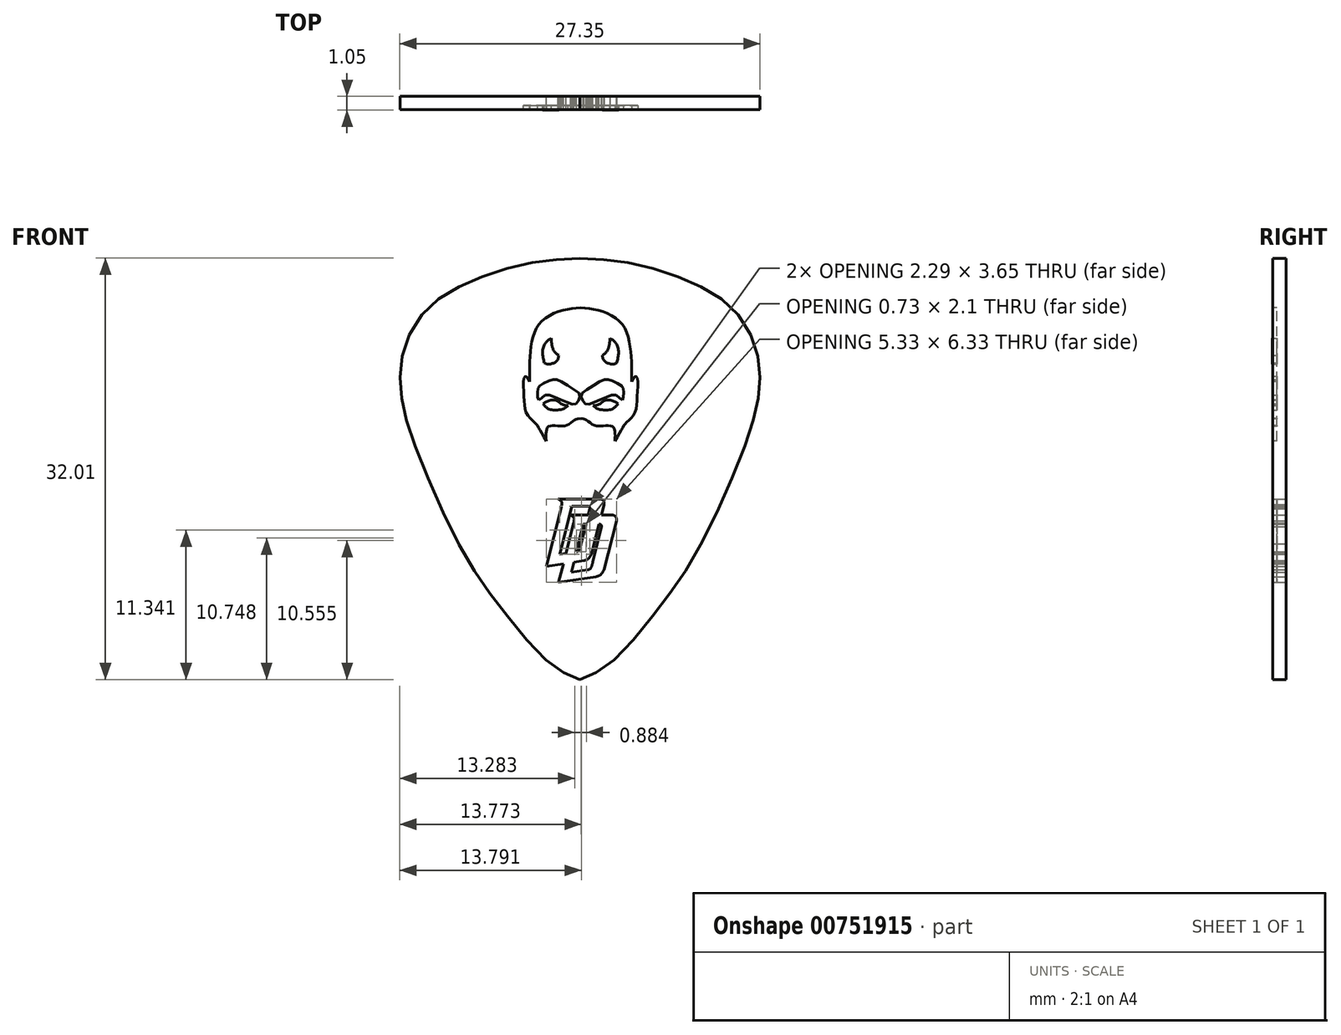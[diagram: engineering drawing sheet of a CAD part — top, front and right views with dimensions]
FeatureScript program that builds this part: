
annotation { "Feature Type Name" : "Feature", "Feature Type Description" : "" }
export const myFeature = defineFeature(function(context is Context, id is Id, definition is map)
    precondition{}
    {
        {
            var Q0;
            Q0=qCreatedBy(makeId("Front.planeOp"),FACE);
            var sketch = newSketch(context, id + "F0", { "sketchPlane" : qUnion([Q0])});
            skFitSpline(sketch, "E0.MirrorCS", {"points": [v(-31.51, -10.9) * mm, v(-29.34, -9.79) * mm, v(-25.56, -5.52) * mm, v(-22.46, -0.91) * mm, v(-18.88, 7.14) * mm, v(-17.9, 10.9) * mm, v(-18.08, 14) * mm, v(-19.85, 17.2) * mm, v(-23.08, 19.28) * mm, v(-27.51, 20.7) * mm, v(-31.51, 21.1) * mm], "startDerivative": vector(27.97, 10.13) * mm, "endDerivative": vector(-41.25, 2.12) * mm});
            skFitSpline(sketch, "E1.MirrorCS", {"points": [v(-31.51, -10.9) * mm, v(-33.68, -9.79) * mm, v(-37.46, -5.52) * mm, v(-40.56, -0.91) * mm, v(-44.14, 7.14) * mm, v(-45.12, 10.9) * mm, v(-44.94, 14) * mm, v(-43.17, 17.2) * mm, v(-39.94, 19.28) * mm, v(-35.5, 20.7) * mm, v(-31.51, 21.1) * mm], "startDerivative": vector(-27.97, 10.13) * mm, "endDerivative": vector(41.25, 2.12) * mm});
            skSolve(sketch);
        }
        {
            var Q0;
            Q0 = qSketchRegion(id + "F0", true);
            var Q1;
            Q1=makeQuery(id+"F0.imprint","IMPRINT",FACE,{"disambiguationData":[TD([[makeQuery(id+"F0.imprint","IMPRINT",EDGE,{"derivedFrom":sQuery(id+"F0.wireOp",EDGE,"E0.MirrorCS")}),1.0]])]});
            extrude(context, id + "F1", {"entities" : qUnion([Q0, Q1]), "depth" : 1 * mm, "offsetDistance" : 25.4 * mm});
        }
        {
            var Q0;
            Q0=qCreatedBy(makeId("Front.planeOp"),FACE);
            var sketch = newSketch(context, id + "F2", { "sketchPlane" : qUnion([Q0])});
            skLineSegment(sketch, "E2", {"start": v(-33.17, 2.8) * mm, "end": v(-30.14, 2.8) * mm});
            skFitSpline(sketch, "E3", {"points": [v(-33.17, 2.8) * mm, v(-32.99, 2.69) * mm, v(-32.9, 2.56) * mm, v(-32.92, 2.2) * mm], "startDerivative": vector(0.59, -0.39) * mm, "endDerivative": vector(-0.18, -0.99) * mm});
            skLineSegment(sketch, "E4", {"start": v(-32.92, 2.2) * mm, "end": v(-34.07, -2.3) * mm});
            skLineSegment(sketch, "E5", {"start": v(-29.68, 2.37) * mm, "end": v(-29.87, 1.6) * mm});
            skFitSpline(sketch, "E6", {"points": [v(-29.68, 2.37) * mm, v(-29.68, 2.56) * mm, v(-29.81, 2.75) * mm, v(-30.14, 2.8) * mm], "startDerivative": vector(0.08, 0.64) * mm, "endDerivative": vector(-0.94, 0.02) * mm});
            skLineSegment(sketch, "E7", {"start": v(-34.07, -2.3) * mm, "end": v(-32.77, -2.11) * mm});
            skFitSpline(sketch, "E8", {"points": [v(-31.2, -1.88) * mm, v(-30.9, -1.75) * mm, v(-30.62, -1.35) * mm], "startDerivative": vector(0.73, 0.2) * mm, "endDerivative": vector(0.45, 0.85) * mm});
            skLineSegment(sketch, "E9", {"start": v(-32.23, 1.6) * mm, "end": v(-30.88, 1.6) * mm});
            skFitSpline(sketch, "E10", {"points": [v(-32.23, 1.6) * mm, v(-32.05, 1.47) * mm, v(-31.96, 1.35) * mm, v(-31.98, 1) * mm], "startDerivative": vector(0.59, -0.39) * mm, "endDerivative": vector(-0.18, -0.99) * mm});
            skLineSegment(sketch, "E11", {"start": v(-31.98, 1) * mm, "end": v(-32.57, -1.33) * mm});
            skLineSegment(sketch, "E12", {"start": v(-28.74, 1.16) * mm, "end": v(-29.68, -2.56) * mm});
            skFitSpline(sketch, "E13", {"points": [v(-28.74, 1.16) * mm, v(-28.74, 1.35) * mm, v(-28.88, 1.54) * mm, v(-29.2, 1.6) * mm], "startDerivative": vector(0.08, 0.64) * mm, "endDerivative": vector(-0.94, 0.02) * mm});
            skLineSegment(sketch, "E14", {"start": v(-33.13, -3.52) * mm, "end": v(-30.27, -3.1) * mm});
            skFitSpline(sketch, "E15", {"points": [v(-30.27, -3.1) * mm, v(-29.95, -2.96) * mm, v(-29.68, -2.56) * mm], "startDerivative": vector(0.73, 0.2) * mm, "endDerivative": vector(0.45, 0.85) * mm});
            skLineSegment(sketch, "E16", {"start": v(-32.14, 2.25) * mm, "end": v(-33.05, -1.4) * mm});
            skLineSegment(sketch, "E17", {"start": v(-33.05, -1.4) * mm, "end": v(-32.57, -1.33) * mm});
            skFitSpline(sketch, "E18", {"points": [v(-31.82, -1.22) * mm, v(-31.65, -1.17) * mm, v(-31.5, -0.94) * mm, v(-31.41, -0.6) * mm], "startDerivative": vector(0.63, 0.09) * mm, "endDerivative": vector(0.2, 0.9) * mm});
            skLineSegment(sketch, "E19", {"start": v(-31.41, -0.6) * mm, "end": v(-31.05, 0.89) * mm});
            skLineSegment(sketch, "E20", {"start": v(-32.14, 2.25) * mm, "end": v(-30.94, 2.25) * mm});
            skFitSpline(sketch, "E21", {"points": [v(-30.77, 2.07) * mm, v(-30.77, 2.15) * mm, v(-30.83, 2.24) * mm, v(-30.94, 2.25) * mm], "startDerivative": vector(0.04, 0.26) * mm, "endDerivative": vector(-0.34, 0) * mm});
            skLineSegment(sketch, "E22", {"start": v(-31.25, 0.89) * mm, "end": v(-31.78, -1.21) * mm});
            skLineSegment(sketch, "E23", {"start": v(-32.17, -2.76) * mm, "end": v(-30.93, -2.58) * mm});
            skFitSpline(sketch, "E24", {"points": [v(-30.93, -2.58) * mm, v(-30.77, -2.53) * mm, v(-30.63, -2.31) * mm, v(-30.53, -1.97) * mm], "startDerivative": vector(0.63, 0.09) * mm, "endDerivative": vector(0.2, 0.9) * mm});
            skLineSegment(sketch, "E25", {"start": v(-30.53, -1.97) * mm, "end": v(-29.88, 0.7) * mm});
            skLineSegment(sketch, "E26", {"start": v(-31.25, 0.89) * mm, "end": v(-31.05, 0.89) * mm});
            skFitSpline(sketch, "E27", {"points": [v(-29.88, 0.7) * mm, v(-29.88, 0.79) * mm, v(-29.94, 0.87) * mm, v(-30.06, 0.89) * mm], "startDerivative": vector(0.04, 0.26) * mm, "endDerivative": vector(-0.34, 0) * mm});
            skLineSegment(sketch, "E28.trimOffspring", {"start": v(-31.98, -2) * mm, "end": v(-32.17, -2.76) * mm});
            skLineSegment(sketch, "E29.trimOffspring", {"start": v(-32.77, -2.11) * mm, "end": v(-33.13, -3.52) * mm});
            skLineSegment(sketch, "E30.trimOffspring", {"start": v(-31.98, -2) * mm, "end": v(-31.2, -1.88) * mm});
            skLineSegment(sketch, "E31.trimOffspring", {"start": v(-30.88, 1.6) * mm, "end": v(-30.77, 2.07) * mm});
            skLineSegment(sketch, "E32.trimOffspring", {"start": v(-29.87, 1.6) * mm, "end": v(-29.2, 1.6) * mm});
            skLineSegment(sketch, "E33.trimOffspring", {"start": v(-30.05, 0.89) * mm, "end": v(-30.62, -1.35) * mm});
            skSolve(sketch);
        }
        {
            var Q0;
            Q0 = qSketchRegion(id + "F2", true);
            extrude(context, id + "F3", {"entities" : qUnion([Q0]), "operationType" : NewBodyOperationType.REMOVE, "endBound" : BoundingType.THROUGH_ALL, "depth" : 25.4 * mm, "offsetDistance" : 25.4 * mm, "hasSecondDirection" : true, "secondDirectionOppositeDirection" : true, "secondDirectionDepth" : .2 * mm});
        }
        {
            var Q0;
            {var subQ0=sQuery(id+"F0.wireOp",EDGE,"E1.MirrorCS");var subQ1=sQuery(id+"F0.wireOp",EDGE,"E0.MirrorCS");Q0=makeQuery(id+"F3.boolean.opBoolean","SPLIT",FACE,{"disambiguationData":[TD([makeQuery(id+"F1.opExtrude","SWEPT_FACE",FACE,{"disambiguationData":[OSD([subQ1])]})])],"derivedFrom":makeQuery(id+"F1.opExtrude","CAP_FACE",FACE,{"disambiguationData":[OSD([subQ1,subQ0])],"isStart":false})});}
            var sketch = newSketch(context, id + "F4", { "sketchPlane" : qUnion([Q0])});
            skFitSpline(sketch, "E34", {"points": [v(-34.07, 7.22) * mm, v(-34.62, 8.16) * mm, v(-34.8, 8.44) * mm, v(-35.12, 8.77) * mm, v(-35.6, 9.37) * mm, v(-35.75, 10.44) * mm, v(-35.79, 11.87) * mm, v(-35.64, 12.13) * mm, v(-35.33, 11.72) * mm], "startDerivative": vector(-4.06, 6.89) * mm, "endDerivative": vector(3.02, -5.65) * mm});
            skFitSpline(sketch, "E35", {"points": [v(-35.33, 11.72) * mm, v(-35.33, 12.86) * mm, v(-35.17, 14.74) * mm, v(-34.5, 16.22) * mm, v(-32.98, 17.1) * mm, v(-31.46, 17.34) * mm], "startDerivative": vector(-0.08, 6.2) * mm, "endDerivative": vector(7.58, 0.61) * mm});
            skFitSpline(sketch, "E36.MirrorCS", {"points": [v(-27.59, 11.72) * mm, v(-27.59, 12.86) * mm, v(-27.76, 14.74) * mm, v(-28.43, 16.22) * mm, v(-29.94, 17.1) * mm, v(-31.46, 17.34) * mm], "startDerivative": vector(0.08, 6.2) * mm, "endDerivative": vector(-7.58, 0.61) * mm});
            skFitSpline(sketch, "E37.MirrorCS", {"points": [v(-28.85, 7.22) * mm, v(-28.3, 8.16) * mm, v(-28.13, 8.44) * mm, v(-27.8, 8.77) * mm, v(-27.33, 9.37) * mm, v(-27.17, 10.44) * mm, v(-27.13, 11.87) * mm, v(-27.28, 12.13) * mm, v(-27.59, 11.72) * mm], "startDerivative": vector(4.06, 6.89) * mm, "endDerivative": vector(-3.02, -5.65) * mm});
            skFitSpline(sketch, "E38", {"points": [v(-34.07, 7.22) * mm, v(-34.07, 7.92) * mm, v(-33.92, 8.29) * mm, v(-33.34, 8.37) * mm, v(-32.67, 8.36) * mm, v(-32.1, 8.65) * mm, v(-31.72, 8.9) * mm, v(-31.46, 8.9) * mm], "startDerivative": vector(-0.18, 4.45) * mm, "endDerivative": vector(2.53, -0.4) * mm});
            skFitSpline(sketch, "E39.MirrorCS", {"points": [v(-28.85, 7.22) * mm, v(-28.85, 7.92) * mm, v(-29, 8.29) * mm, v(-29.58, 8.37) * mm, v(-30.26, 8.36) * mm, v(-30.82, 8.65) * mm, v(-31.2, 8.9) * mm, v(-31.46, 8.9) * mm], "startDerivative": vector(0.18, 4.45) * mm, "endDerivative": vector(-2.53, -0.4) * mm});
            skSolve(sketch);
        }
        {
            var Q0;
            Q0 = qSketchRegion(id + "F4", true);
            extrude(context, id + "F5", {"entities" : qUnion([Q0]), "operationType" : NewBodyOperationType.REMOVE, "oppositeDirection" : true, "depth" : .3 * mm, "offsetDistance" : 25 * mm});
        }
        {
            var Q0;
            Q0=makeQuery(id+"F5.boolean.opBoolean","COPY",FACE,{"derivedFrom":makeQuery(id+"F5.opExtrude","CAP_FACE",FACE,{"disambiguationData":[OSD([sQuery(id+"F4.wireOp",EDGE,"E34"),sQuery(id+"F4.wireOp",EDGE,"E35"),sQuery(id+"F4.wireOp",EDGE,"E36.MirrorCS"),sQuery(id+"F4.wireOp",EDGE,"E37.MirrorCS"),sQuery(id+"F4.wireOp",EDGE,"E38"),sQuery(id+"F4.wireOp",EDGE,"E39.MirrorCS")])],"isStart":false})});
            var sketch = newSketch(context, id + "F6", { "sketchPlane" : qUnion([Q0])});
            skFitSpline(sketch, "E40", {"points": [v(-33.12, 13.73) * mm, v(-33.52, 14.1) * mm, v(-33.7, 15.01) * mm], "startDerivative": vector(-1.04, 0.7) * mm, "endDerivative": vector(-0.15, 1.82) * mm});
            skFitSpline(sketch, "E41", {"points": [v(-33.7, 15.01) * mm, v(-34.13, 14.66) * mm, v(-34.35, 14) * mm, v(-34.2, 13.13) * mm], "startDerivative": vector(-1.6, -1.02) * mm, "endDerivative": vector(0.6, -2.38) * mm});
            skFitSpline(sketch, "E42", {"points": [v(-34.2, 13.13) * mm, v(-33.97, 13.06) * mm, v(-33.51, 13.13) * mm, v(-33.19, 13.4) * mm, v(-33.12, 13.73) * mm], "startDerivative": vector(1.03, -0.49) * mm, "endDerivative": vector(0.1, 1.39) * mm});
            skFitSpline(sketch, "E43.MirrorCS", {"points": [v(-29.8, 13.73) * mm, v(-29.4, 14.1) * mm, v(-29.23, 15.01) * mm], "startDerivative": vector(1.04, 0.7) * mm, "endDerivative": vector(0.15, 1.82) * mm});
            skFitSpline(sketch, "E44.MirrorCS", {"points": [v(-29.23, 15.01) * mm, v(-28.8, 14.66) * mm, v(-28.57, 14) * mm, v(-28.71, 13.13) * mm], "startDerivative": vector(1.6, -1.02) * mm, "endDerivative": vector(-0.6, -2.38) * mm});
            skFitSpline(sketch, "E45.MirrorCS", {"points": [v(-28.71, 13.13) * mm, v(-28.95, 13.06) * mm, v(-29.4, 13.13) * mm, v(-29.73, 13.4) * mm, v(-29.8, 13.73) * mm], "startDerivative": vector(-1.03, -0.49) * mm, "endDerivative": vector(-0.1, 1.39) * mm});
            skSolve(sketch);
        }
        {
            var Q0;
            Q0=makeQuery(id+"F6.imprint","IMPRINT",FACE,{"disambiguationData":[TD([[makeQuery(id+"F6.imprint","IMPRINT",EDGE,{"derivedFrom":sQuery(id+"F6.wireOp",EDGE,"E43.MirrorCS")}),-1.0]])]});
            var Q1;
            Q1=makeQuery(id+"F6.imprint","IMPRINT",FACE,{"disambiguationData":[TD([[makeQuery(id+"F6.imprint","IMPRINT",EDGE,{"derivedFrom":sQuery(id+"F6.wireOp",EDGE,"E40")}),1.0]])]});
            extrude(context, id + "F7", {"entities" : qUnion([Q0, Q1]), "operationType" : NewBodyOperationType.ADD, "depth" : .35 * mm, "offsetDistance" : 25 * mm});
        }
        {
            var Q0;
            Q0=makeQuery(id+"F5.boolean.opBoolean","COPY",FACE,{"derivedFrom":makeQuery(id+"F5.opExtrude","CAP_FACE",FACE,{"disambiguationData":[OSD([sQuery(id+"F4.wireOp",EDGE,"E34"),sQuery(id+"F4.wireOp",EDGE,"E35"),sQuery(id+"F4.wireOp",EDGE,"E36.MirrorCS"),sQuery(id+"F4.wireOp",EDGE,"E37.MirrorCS"),sQuery(id+"F4.wireOp",EDGE,"E38"),sQuery(id+"F4.wireOp",EDGE,"E39.MirrorCS")])],"isStart":false})});
            var sketch = newSketch(context, id + "F8", { "sketchPlane" : qUnion([Q0])});
            skFitSpline(sketch, "E46", {"points": [v(-28.3, 10.31) * mm, v(-28.53, 10.5) * mm, v(-28.87, 10.71) * mm, v(-29.4, 10.59) * mm, v(-30.27, 10.22) * mm, v(-30.93, 9.99) * mm, v(-31.2, 10.13) * mm, v(-31.39, 10.47) * mm, v(-31.38, 10.79) * mm, v(-30.72, 11.28) * mm, v(-29.8, 11.82) * mm, v(-29.43, 11.89) * mm, v(-29.03, 11.78) * mm, v(-28.45, 11.48) * mm, v(-28.26, 11.3) * mm, v(-28.19, 11) * mm, v(-28.2, 10.5) * mm, v(-28.3, 10.31) * mm]});
            skFitSpline(sketch, "E47.MirrorC", {"points": [v(-34.62, 10.31) * mm, v(-34.39, 10.5) * mm, v(-34.05, 10.71) * mm, v(-33.53, 10.59) * mm, v(-32.65, 10.22) * mm, v(-32, 9.99) * mm, v(-31.72, 10.13) * mm, v(-31.53, 10.47) * mm, v(-31.54, 10.79) * mm, v(-32.2, 11.28) * mm, v(-33.13, 11.82) * mm, v(-33.5, 11.89) * mm, v(-33.9, 11.78) * mm, v(-34.47, 11.48) * mm, v(-34.66, 11.3) * mm, v(-34.73, 11) * mm, v(-34.71, 10.5) * mm, v(-34.62, 10.31) * mm]});
            skSolve(sketch);
        }
        {
            var Q0;
            Q0=makeQuery(id+"F8.imprint","IMPRINT",FACE,{"disambiguationData":[TD([[makeQuery(id+"F8.imprint","IMPRINT",EDGE,{"derivedFrom":sQuery(id+"F8.wireOp",EDGE,"E46")}),-1.0]])]});
            var Q1;
            Q1=makeQuery(id+"F8.imprint","IMPRINT",FACE,{"disambiguationData":[TD([[makeQuery(id+"F8.imprint","IMPRINT",EDGE,{"derivedFrom":sQuery(id+"F8.wireOp",EDGE,"E47.MirrorC")}),1.0]])]});
            extrude(context, id + "F9", {"entities" : qUnion([Q0, Q1]), "operationType" : NewBodyOperationType.ADD, "depth" : .3 * mm, "offsetDistance" : 25 * mm});
        }
        {
            var Q0;
            Q0=makeQuery(id+"F5.boolean.opBoolean","COPY",FACE,{"derivedFrom":makeQuery(id+"F5.opExtrude","CAP_FACE",FACE,{"disambiguationData":[OSD([sQuery(id+"F4.wireOp",EDGE,"E34"),sQuery(id+"F4.wireOp",EDGE,"E35"),sQuery(id+"F4.wireOp",EDGE,"E36.MirrorCS"),sQuery(id+"F4.wireOp",EDGE,"E37.MirrorCS"),sQuery(id+"F4.wireOp",EDGE,"E38"),sQuery(id+"F4.wireOp",EDGE,"E39.MirrorCS")])],"isStart":false})});
            var sketch = newSketch(context, id + "F10", { "sketchPlane" : qUnion([Q0])});
            skFitSpline(sketch, "E48", {"points": [v(-34.3, 10.02) * mm, v(-34.18, 9.88) * mm, v(-34.02, 9.73) * mm, v(-33.81, 9.61) * mm, v(-33.4, 9.57) * mm, v(-33.03, 9.58) * mm, v(-32.77, 9.64) * mm, v(-32.4, 9.9) * mm], "startDerivative": vector(1.06, -1.28) * mm, "endDerivative": vector(2.22, 1.76) * mm});
            skFitSpline(sketch, "E49", {"points": [v(-34.3, 10.02) * mm, v(-34.13, 10.16) * mm, v(-33.91, 10.26) * mm, v(-33.58, 10.33) * mm, v(-33.22, 10.24) * mm, v(-33.01, 10.1) * mm, v(-32.74, 9.96) * mm, v(-32.4, 9.9) * mm], "startDerivative": vector(1.36, 1.2) * mm, "endDerivative": vector(2.27, -0.26) * mm});
            skFitSpline(sketch, "E50.MirrorCS", {"points": [v(-28.61, 10.02) * mm, v(-28.8, 10.16) * mm, v(-29, 10.26) * mm, v(-29.34, 10.33) * mm, v(-29.7, 10.24) * mm, v(-29.91, 10.1) * mm, v(-30.18, 9.96) * mm, v(-30.52, 9.9) * mm], "startDerivative": vector(-1.36, 1.2) * mm, "endDerivative": vector(-2.27, -0.26) * mm});
            skFitSpline(sketch, "E51.MirrorCS", {"points": [v(-28.61, 10.02) * mm, v(-28.74, 9.88) * mm, v(-28.9, 9.73) * mm, v(-29.1, 9.61) * mm, v(-29.52, 9.57) * mm, v(-29.9, 9.58) * mm, v(-30.15, 9.64) * mm, v(-30.52, 9.9) * mm], "startDerivative": vector(-1.06, -1.28) * mm, "endDerivative": vector(-2.22, 1.76) * mm});
            skSolve(sketch);
        }
        {
            var Q0;
            Q0 = qSketchRegion(id + "F10", true);
            extrude(context, id + "F11", {"entities" : qUnion([Q0]), "operationType" : NewBodyOperationType.ADD, "depth" : .1 * mm, "offsetDistance" : 25 * mm});
        }
        {
            var Q0;
            Q0 = qSketchRegion(id + "F10", true);
            var Q1;
            Q1=makeQuery(id+"F11.opExtrude","CAP_FACE",FACE,{"disambiguationData":[OSD([sQuery(id+"F10.wireOp",EDGE,"E48"),sQuery(id+"F10.wireOp",EDGE,"E49")])],"isStart":false});
            var Q2;
            Q2=makeQuery(id+"F11.opExtrude","CAP_FACE",FACE,{"disambiguationData":[OSD([sQuery(id+"F10.wireOp",EDGE,"E50.MirrorCS"),sQuery(id+"F10.wireOp",EDGE,"E51.MirrorCS")])],"isStart":false});
            extrude(context, id + "F12", {"entities" : qUnion([Q0, Q1, Q2]), "operationType" : NewBodyOperationType.ADD, "depth" : .2 * mm, "offsetDistance" : 25 * mm});
        }
        {
            var Q0;
            Q0 = qSketchRegion(id + "F2", true);
            extrude(context, id + "F13", {"entities" : qUnion([Q0]), "depth" : .7 * mm, "offsetDistance" : 25 * mm});
        }
    });
